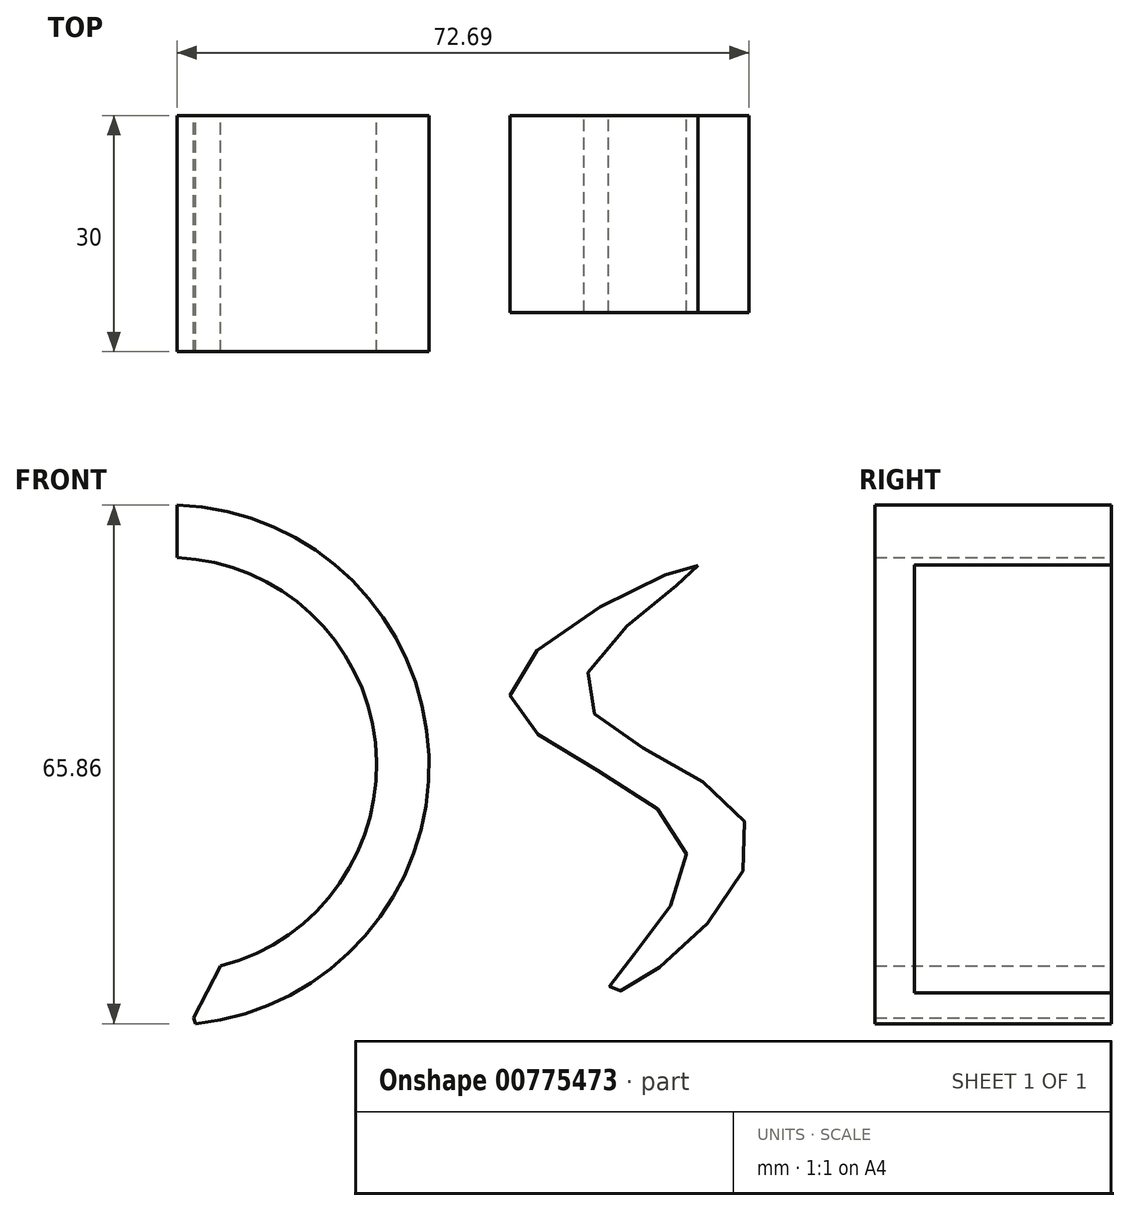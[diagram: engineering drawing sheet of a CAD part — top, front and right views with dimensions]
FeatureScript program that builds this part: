
annotation { "Feature Type Name" : "Feature", "Feature Type Description" : "" }
export const myFeature = defineFeature(function(context is Context, id is Id, definition is map)
    precondition{}
    {
        {
            var Q0;
            Q0=qCreatedBy(makeId("Front.planeOp"),FACE);
            var sketch = newSketch(context, id + "F0", { "sketchPlane" : qUnion([Q0])});
            skArc(sketch, "E0", {"start": v(-19, 33.01) * mm, "mid": v(13, 1.19) * mm, "end": v(-16.64, -32.85) * mm});
            skArc(sketch, "E1", {"start": v(-19, 26.34) * mm, "mid": v(6.35, 0) * mm, "end": v(-19, -26.34) * mm});
            skLineSegment(sketch, "E2", {"start": v(-19, 26.34) * mm, "end": v(-19, 33.01) * mm});
            skLineSegment(sketch, "E3", {"start": v(-19, -26.34) * mm, "end": v(-16.64, -32.85) * mm});
            skSolve(sketch);
        }
        {
            var Q0;
            Q0 = qSketchRegion(id + "F0", true);
            extrude(context, id + "F1", {"entities" : qUnion([Q0]), "depth" : 30 * mm, "offsetDistance" : 25 * mm});
        }
        {
            var Q0;
            Q0=qCreatedBy(makeId("Front.planeOp"),FACE);
            var sketch = newSketch(context, id + "F2", { "sketchPlane" : qUnion([Q0])});
            skFitSpline(sketch, "E4", {"points": [v(47.18, 25.34) * mm, v(32.68, 9.84) * mm, v(53.35, -7.84) * mm, v(38.18, -28.34) * mm, v(35.84, -28.34) * mm, v(45.51, -10.17) * mm, v(23.34, 9.5) * mm, v(47.18, 25.34) * mm]});
            skSolve(sketch);
        }
        {
            var Q0;
            Q0 = qSketchRegion(id + "F2", true);
            extrude(context, id + "F3", {"entities" : qUnion([Q0]), "depth" : 25 * mm, "offsetDistance" : 25 * mm});
        }
        {
            var Q0;
            Q0=makeQuery(id+"F1.opExtrude","SWEPT_EDGE",EDGE,{"disambiguationData":[OSD([sQuery(id+"F0.wireOp",EDGE,"E1"),sQuery(id+"F0.wireOp",EDGE,"E3")])]});
            chamfer(context, id + "F4", {"entities" : qUnion([Q0]), "width" : 5 * mm, "tangentPropagation" : true});
        }
    });
